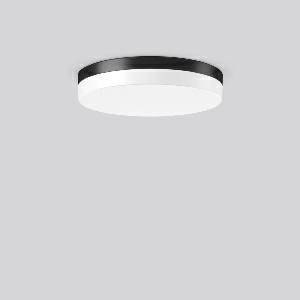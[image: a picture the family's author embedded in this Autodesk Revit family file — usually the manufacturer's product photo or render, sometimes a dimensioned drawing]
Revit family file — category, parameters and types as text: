
# Revit family: flat_slim_round_312676_0031_1_19_275e
name_source: partatom
category: Lighting Fixtures
units: mm (PartAtom-declared; Revit-internal decimal feet)

## family parameters
Cut with Voids When Loaded = No
Host = Face
Light Source = No
Part Type = Normal
Room Calculation Point = No
Round Connector Dimension = Use Diameter
Shared = No

## types (1)
- MultiLumen 1 830 (1 x LED Modul 830, 2450 lm, 3000)
    Apparent Load = 18 VA
    CIE Flux Codes = 37 67 88 84 100
    Color Rendering = 80
    Color Temperature = 3000
    Default Elevation = 1800 mm
    Height = 70 mm
    Lamp = 1 x LED Modul 830
    Lamp Light Flux = 2450 lm
    Lamp count = 1
    Length = 400 mm
    Lifetime = 50000 h
    Luminous efficacy = 136 lm/W
    Manufacturer = RZB
    ModVariant = No
    Model = 312676.0031.1.19
    Mounting Place = Ceiling
    Mounting Type = Surface mounted
    Number of Poles = 1
    OnlyDefault = Yes
    Power Factor = 1
    Product Name = FLAT SLIM round
    Product group = Surface mounted ceiling and wall luminaires
    ProductGroupID = 305
    Protection Class = Protection class I
    Protection Degree = Degree of protection
    RLX_Detail_Level = 1
    RLX_Emergency_Light_Flux = 0 lm
    RLX_Emergency_Type = 0
    RLX_Emergency_Type_DB = No
    RlxData = <blob elided: 22045 chars, md5=7deeea2c>
    Socket = socket
    Standby Power = 0 W
    System Light Flux = 2450 lm
    System Power = 18 W
    Type Comments = MultiLumen 1 830
    Type Image = 312631.0031.jpg
    URL = http://relux.com
    VarID = multilumen_1_830
    Voltage = 0 V
    Weight = 0.00 kg
    Width = 0 mm  [stored 0 ft]

note: [stored X ft] marks values corroborated as IEEE doubles in the binary element streams (Revit-internal decimal feet)

## geometry (parser evidence)
native form markers: Blend x4, Sweep x14
no freeform markers — native parametric forms only
